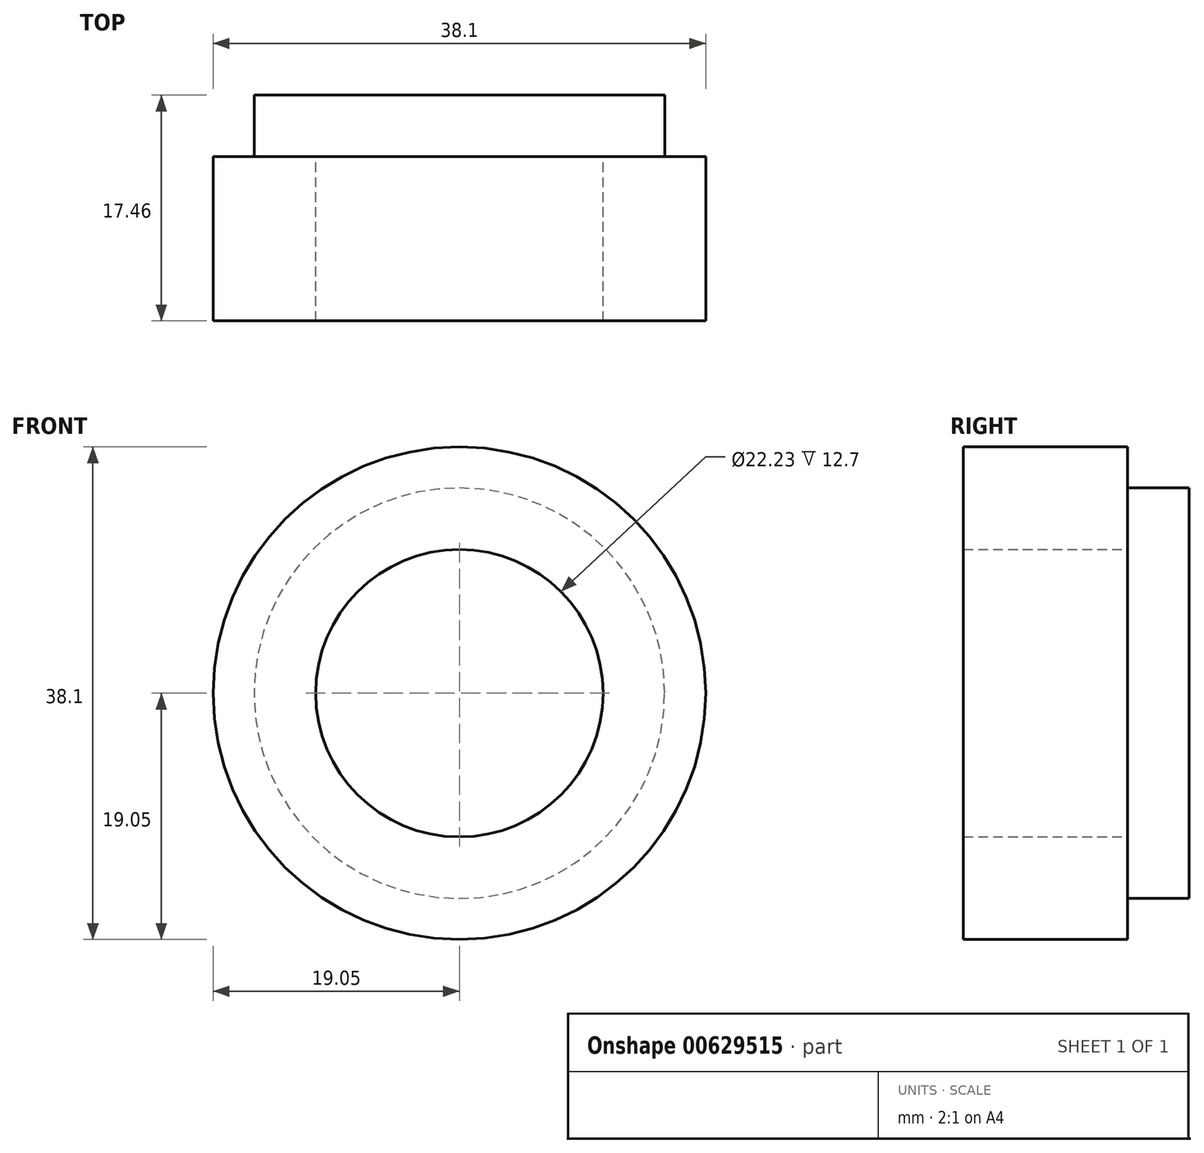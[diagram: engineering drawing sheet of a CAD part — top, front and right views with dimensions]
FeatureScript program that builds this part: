
annotation { "Feature Type Name" : "Feature", "Feature Type Description" : "" }
export const myFeature = defineFeature(function(context is Context, id is Id, definition is map)
    precondition{}
    {
        {
            var Q0;
            Q0=qCreatedBy(makeId("Front.planeOp"),FACE);
            var sketch = newSketch(context, id + "F0", { "sketchPlane" : qUnion([Q0])});
            skCircle(sketch, "E0", {"center": v(0, 0) * mm, "radius": 11.11 * mm});
            skCircle(sketch, "E1", {"center": v(0, 0) * mm, "radius": 19.05 * mm});
            skSolve(sketch);
        }
        {
            var Q0;
            Q0=qSketchRegion(id+"F0",true);
            extrude(context, id + "F1", {"entities" : qUnion([Q0]), "depth" : 12.7 * mm});
        }
        {
            var Q0;
            Q0=makeQuery(id+"F1.opExtrude","CAP_FACE",FACE,{"disambiguationData":[OSD([sQuery(id+"F0.wireOp",EDGE,"E0"),sQuery(id+"F0.wireOp",EDGE,"E1")])],"isStart":true});
            var sketch = newSketch(context, id + "F2", { "sketchPlane" : qUnion([Q0])});
            skCircle(sketch, "E2", {"center": v(0, 0) * mm, "radius": 15.88 * mm});
            skSolve(sketch);
        }
        {
            var Q0;
            Q0=qSketchRegion(id+"F2",true);
            extrude(context, id + "F3", {"entities" : qUnion([Q0]), "operationType" : NewBodyOperationType.ADD, "depth" : 4.76 * mm});
        }
    });
